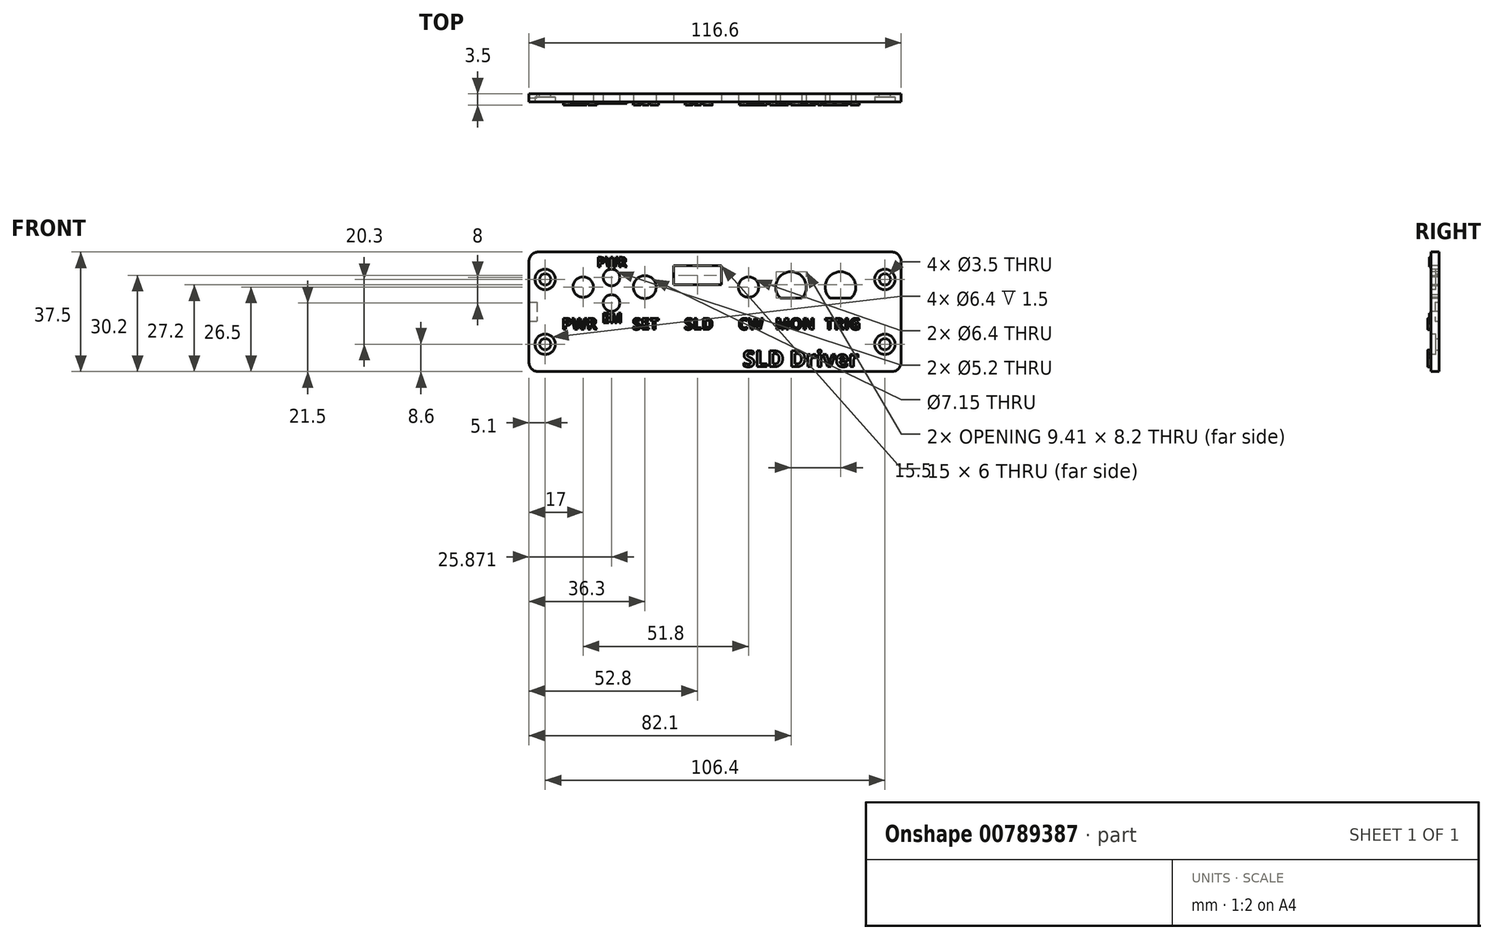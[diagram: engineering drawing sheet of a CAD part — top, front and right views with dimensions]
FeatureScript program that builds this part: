
annotation { "Feature Type Name" : "Feature", "Feature Type Description" : "" }
export const myFeature = defineFeature(function(context is Context, id is Id, definition is map)
    precondition{}
    {
        {
            var Q0;
            Q0=qCreatedBy(makeId("Front.planeOp"),FACE);
            var sketch = newSketch(context, id + "F0", { "sketchPlane" : qUnion([Q0])});
            skLineSegment(sketch, "E0.bottom", {"start": v(-55.3, 18.75) * mm, "end": v(55.3, 18.75) * mm});
            skLineSegment(sketch, "E0.top", {"start": v(-55.3, -18.75) * mm, "end": v(55.3, -18.75) * mm});
            skLineSegment(sketch, "E0.left", {"start": v(-58.3, 15.75) * mm, "end": v(-58.3, -15.75) * mm});
            skLineSegment(sketch, "E0.right", {"start": v(58.3, 15.75) * mm, "end": v(58.3, -15.75) * mm});
            skPoint(sketch, "E1.visualSharp", {"position": v(-58.3, 18.75) * mm});
            skArc(sketch, "E1.filletArc", {"start": v(-55.3, 18.75) * mm, "mid": v(-57.42, 17.87) * mm, "end": v(-58.3, 15.75) * mm});
            skPoint(sketch, "E2.visualSharp", {"position": v(58.3, 18.75) * mm});
            skArc(sketch, "E2.filletArc", {"start": v(58.3, 15.75) * mm, "mid": v(57.42, 17.87) * mm, "end": v(55.3, 18.75) * mm});
            skPoint(sketch, "E3.visualSharp", {"position": v(58.3, -18.75) * mm});
            skArc(sketch, "E3.filletArc", {"start": v(55.3, -18.75) * mm, "mid": v(57.42, -17.87) * mm, "end": v(58.3, -15.75) * mm});
            skPoint(sketch, "E4.visualSharp", {"position": v(-58.3, -18.75) * mm});
            skArc(sketch, "E4.filletArc", {"start": v(-58.3, -15.75) * mm, "mid": v(-57.42, -17.87) * mm, "end": v(-55.3, -18.75) * mm});
            skCircle(sketch, "E5", {"center": v(-53.2, 10.15) * mm, "radius": 1.75 * mm});
            skCircle(sketch, "E6", {"center": v(53.2, 10.15) * mm, "radius": 1.75 * mm});
            skCircle(sketch, "E7", {"center": v(-53.2, -10.15) * mm, "radius": 1.75 * mm});
            skCircle(sketch, "E8", {"center": v(53.2, -10.15) * mm, "radius": 1.75 * mm});
            skSolve(sketch);
        }
        {
            var Q0;
            Q0=makeQuery(id+"F0.imprint","IMPRINT",FACE,{"disambiguationData":[TD([[makeQuery(id+"F0.imprint","IMPRINT",EDGE,{"derivedFrom":sQuery(id+"F0.wireOp",EDGE,"E0.bottom")}),-1.0]])]});
            extrude(context, id + "F1", {"entities" : qUnion([Q0]), "depth" : 2.5 * mm});
        }
        {
            var Q0;
            Q0=makeQuery(id+"F1.opExtrude","CAP_FACE",FACE,{"disambiguationData":[OSD([sQuery(id+"F0.wireOp",EDGE,"E0.bottom"),sQuery(id+"F0.wireOp",EDGE,"E0.top"),sQuery(id+"F0.wireOp",EDGE,"E0.left"),sQuery(id+"F0.wireOp",EDGE,"E0.right"),sQuery(id+"F0.wireOp",EDGE,"E1.filletArc"),sQuery(id+"F0.wireOp",EDGE,"E2.filletArc"),sQuery(id+"F0.wireOp",EDGE,"E3.filletArc"),sQuery(id+"F0.wireOp",EDGE,"E4.filletArc"),sQuery(id+"F0.wireOp",EDGE,"E5"),sQuery(id+"F0.wireOp",EDGE,"E6"),sQuery(id+"F0.wireOp",EDGE,"E7"),sQuery(id+"F0.wireOp",EDGE,"E8")])],"isStart":false});
            var sketch = newSketch(context, id + "F2", { "sketchPlane" : qUnion([Q0])});
            skCircle(sketch, "E9", {"center": v(-53.2, 10.15) * mm, "radius": 3.2 * mm});
            skCircle(sketch, "E10", {"center": v(53.2, 10.15) * mm, "radius": 3.2 * mm});
            skCircle(sketch, "E11", {"center": v(-53.2, -10.15) * mm, "radius": 3.2 * mm});
            skCircle(sketch, "E12", {"center": v(53.2, -10.15) * mm, "radius": 3.2 * mm});
            skSolve(sketch);
        }
        {
            var Q0;
            Q0=qSketchRegion(id+"F2",true);
            extrude(context, id + "F3", {"entities" : qUnion([Q0]), "operationType" : NewBodyOperationType.REMOVE, "oppositeDirection" : true, "depth" : 1.5 * mm});
        }
        {
            var Q0;
            Q0=makeQuery(id+"F1.opExtrude","CAP_FACE",FACE,{"disambiguationData":[OSD([sQuery(id+"F0.wireOp",EDGE,"E0.bottom"),sQuery(id+"F0.wireOp",EDGE,"E0.top"),sQuery(id+"F0.wireOp",EDGE,"E0.left"),sQuery(id+"F0.wireOp",EDGE,"E0.right"),sQuery(id+"F0.wireOp",EDGE,"E1.filletArc"),sQuery(id+"F0.wireOp",EDGE,"E2.filletArc"),sQuery(id+"F0.wireOp",EDGE,"E3.filletArc"),sQuery(id+"F0.wireOp",EDGE,"E4.filletArc"),sQuery(id+"F0.wireOp",EDGE,"E5"),sQuery(id+"F0.wireOp",EDGE,"E6"),sQuery(id+"F0.wireOp",EDGE,"E7"),sQuery(id+"F0.wireOp",EDGE,"E8")])],"isStart":true});
            var sketch = newSketch(context, id + "F4", { "sketchPlane" : qUnion([Q0])});
            skLineSegment(sketch, "E13.bottom", {"start": v(58.3, 3) * mm, "end": v(55.8, 3) * mm});
            skLineSegment(sketch, "E13.top", {"start": v(58.3, -3) * mm, "end": v(55.8, -3) * mm});
            skLineSegment(sketch, "E13.left", {"start": v(58.3, 3) * mm, "end": v(58.3, -3) * mm});
            skLineSegment(sketch, "E13.right", {"start": v(55.8, 3) * mm, "end": v(55.8, -3) * mm});
            skSolve(sketch);
        }
        {
            var Q0;
            Q0=qSketchRegion(id+"F4",true);
            extrude(context, id + "F5", {"entities" : qUnion([Q0]), "operationType" : NewBodyOperationType.REMOVE, "oppositeDirection" : true, "depth" : 1.25 * mm});
        }
        {
            var Q0;
            Q0=makeQuery(id+"F1.opExtrude","CAP_FACE",FACE,{"disambiguationData":[OSD([sQuery(id+"F0.wireOp",EDGE,"E0.bottom"),sQuery(id+"F0.wireOp",EDGE,"E0.top"),sQuery(id+"F0.wireOp",EDGE,"E0.left"),sQuery(id+"F0.wireOp",EDGE,"E0.right"),sQuery(id+"F0.wireOp",EDGE,"E1.filletArc"),sQuery(id+"F0.wireOp",EDGE,"E2.filletArc"),sQuery(id+"F0.wireOp",EDGE,"E3.filletArc"),sQuery(id+"F0.wireOp",EDGE,"E4.filletArc"),sQuery(id+"F0.wireOp",EDGE,"E5"),sQuery(id+"F0.wireOp",EDGE,"E6"),sQuery(id+"F0.wireOp",EDGE,"E7"),sQuery(id+"F0.wireOp",EDGE,"E8")])],"isStart":false});
            var sketch = newSketch(context, id + "F6", { "sketchPlane" : qUnion([Q0])});
            skLineSegment(sketch, "E14", {"start": v(-63.46, 7.75) * mm, "end": v(64.15, 7.75) * mm, "construction": true});
            skArc(sketch, "E15", {"start": v(42.69, 4.35) * mm, "mid": v(39.3, 12.55) * mm, "end": v(35.91, 4.35) * mm});
            skLineSegment(sketch, "E16", {"start": v(-48.3, 18.75) * mm, "end": v(-48.3, -12.75) * mm, "construction": true});
            skLineSegment(sketch, "E17", {"start": v(48.3, -12.75) * mm, "end": v(48.3, 18.75) * mm, "construction": true});
            skLineSegment(sketch, "E18.trimOffspring", {"start": v(35.91, 4.35) * mm, "end": v(42.69, 4.35) * mm});
            skCircle(sketch, "E19", {"center": v(-22, 7.75) * mm, "radius": 3.58 * mm});
            skPoint(sketch, "E20", {"position": v(0.34, 7.75) * mm});
            skCircle(sketch, "E21", {"center": v(10.5, 7.75) * mm, "radius": 3.2 * mm});
            skLineSegment(sketch, "E22", {"start": v(-71.06, -1.55) * mm, "end": v(67.35, -1.55) * mm, "construction": true});
            skLineSegment(sketch, "E23", {"start": v(-66.45, 8.45) * mm, "end": v(18.57, 8.45) * mm, "construction": true});
            skLineSegment(sketch, "E24.bottom", {"start": v(-13, 8.45) * mm, "end": v(2, 8.45) * mm});
            skLineSegment(sketch, "E24.top", {"start": v(-13, 14.45) * mm, "end": v(2, 14.45) * mm});
            skLineSegment(sketch, "E24.left", {"start": v(-13, 8.45) * mm, "end": v(-13, 14.45) * mm});
            skLineSegment(sketch, "E24.right", {"start": v(2, 8.45) * mm, "end": v(2, 14.45) * mm});
            skArc(sketch, "E25", {"start": v(27.19, 4.35) * mm, "mid": v(23.8, 12.55) * mm, "end": v(20.41, 4.35) * mm});
            skLineSegment(sketch, "E26.trimOffspring", {"start": v(20.41, 4.35) * mm, "end": v(27.19, 4.35) * mm});
            skLineSegment(sketch, "E27", {"start": v(-32.43, 24.6) * mm, "end": v(-32.43, -13.66) * mm, "construction": true});
            skCircle(sketch, "E28", {"center": v(-41.3, 7.75) * mm, "radius": 3.2 * mm});
            skCircle(sketch, "E29", {"center": v(-32.43, 10.75) * mm, "radius": 2.6 * mm});
            skCircle(sketch, "E30", {"center": v(-32.43, 2.75) * mm, "radius": 2.6 * mm});
            skCircle(sketch, "E31", {"center": v(-22, 7.75) * mm, "radius": 5.25 * mm, "construction": true});
            skSolve(sketch);
        }
        {
            var Q0;
            Q0=qSketchRegion(id+"F6",true);
            extrude(context, id + "F7", {"entities" : qUnion([Q0]), "operationType" : NewBodyOperationType.REMOVE, "endBound" : BoundingType.THROUGH_ALL, "oppositeDirection" : true, "depth" : 25 * mm});
        }
        {
            var Q0;
            Q0=makeQuery(id+"F1.opExtrude","CAP_FACE",FACE,{"disambiguationData":[OSD([sQuery(id+"F0.wireOp",EDGE,"E0.bottom"),sQuery(id+"F0.wireOp",EDGE,"E0.top"),sQuery(id+"F0.wireOp",EDGE,"E0.left"),sQuery(id+"F0.wireOp",EDGE,"E0.right"),sQuery(id+"F0.wireOp",EDGE,"E1.filletArc"),sQuery(id+"F0.wireOp",EDGE,"E2.filletArc"),sQuery(id+"F0.wireOp",EDGE,"E3.filletArc"),sQuery(id+"F0.wireOp",EDGE,"E4.filletArc"),sQuery(id+"F0.wireOp",EDGE,"E5"),sQuery(id+"F0.wireOp",EDGE,"E6"),sQuery(id+"F0.wireOp",EDGE,"E7"),sQuery(id+"F0.wireOp",EDGE,"E8")])],"isStart":false});
            var sketch = newSketch(context, id + "F8", { "sketchPlane" : qUnion([Q0])});
            skText(sketch, "E32", { "text": "PWR", "fontName": "OpenSans-Bold.ttf"});
            skLineSegment(sketch, "E33", {"start": v(-84.62, -5.52) * mm, "end": v(84.91, -5.52) * mm, "construction": true});
            skText(sketch, "E34", { "text": "SET", "fontName": "OpenSans-Bold.ttf"});
            skText(sketch, "E35", { "text": "SLD", "fontName": "OpenSans-Bold.ttf"});
            skText(sketch, "E36", { "text": "CW   MON", "fontName": "OpenSans-Bold.ttf"});
            skText(sketch, "E37", { "text": "TRIG", "fontName": "OpenSans-Bold.ttf"});
            const initialGuessF8  = {"E32": [-0.0479, -0.00552, 1, 0, 0.0035], "E34": [-0.02585, -0.00552, 1, 0, 0.0035], "E35": [-0.0096, -0.00552, 1, 0, 0.0035], "E36": [0.00727, -0.00552, 1, 0, 0.0035], "E37": [0.03443, -0.00552, 1, 0, 0.0035]};
            skSetInitialGuess(sketch, initialGuessF8);
            skSolve(sketch);
        }
        {
            var Q0;
            Q0=qSketchRegion(id+"F8",true);
            extrude(context, id + "F9", {"entities" : qUnion([Q0]), "operationType" : NewBodyOperationType.ADD, "depth" : 1 * mm});
        }
        {
            var Q0;
            {var subQ70=sQuery(id+"F0.wireOp",EDGE,"E0.right");var subQ114=sQuery(id+"F0.wireOp",EDGE,"E3.filletArc");var subQ120=sQuery(id+"F0.wireOp",EDGE,"E4.filletArc");var subQ132=sQuery(id+"F0.wireOp",EDGE,"E1.filletArc");var subQ140=sQuery(id+"F0.wireOp",EDGE,"E0.top");var subQ143=sQuery(id+"F0.wireOp",EDGE,"E0.left");var subQ152=sQuery(id+"F0.wireOp",EDGE,"E2.filletArc");var subQ182=sQuery(id+"F0.wireOp",EDGE,"E0.bottom");var subQ183=makeQuery(id+"F1.opExtrude","SWEPT_FACE",FACE,{"disambiguationData":[OSD([subQ182])]});Q0=makeQuery(id+"Fu2jKsRN7ARvOCH_1.boolean.opBoolean","SPLIT",FACE,{"disambiguationData":[TD([subQ183])],"derivedFrom":makeQuery(id+"F9.boolean.opBoolean","SPLIT",FACE,{"disambiguationData":[TD([subQ183])],"derivedFrom":makeQuery(id+"F1.opExtrude","CAP_FACE",FACE,{"disambiguationData":[OSD([subQ182,subQ140,subQ143,subQ70,subQ132,subQ152,subQ114,subQ120,sQuery(id+"F0.wireOp",EDGE,"E5"),sQuery(id+"F0.wireOp",EDGE,"E6"),sQuery(id+"F0.wireOp",EDGE,"E7"),sQuery(id+"F0.wireOp",EDGE,"E8")])],"isStart":false})})});}
            var sketch = newSketch(context, id + "F10", { "sketchPlane" : qUnion([Q0])});
            skText(sketch, "E38", { "text": "SLD Driver", "fontName": "OpenSans-Bold.ttf"});
            const initialGuessF10  = {"E38": [0.00869, -0.0172, 1, 0, 0.005]};
            skSetInitialGuess(sketch, initialGuessF10);
            skSolve(sketch);
        }
        {
            var Q0;
            Q0=qSketchRegion(id+"F10",true);
            extrude(context, id + "F11", {"entities" : qUnion([Q0]), "operationType" : NewBodyOperationType.ADD, "depth" : 1 * mm});
        }
        {
            var Q0;
            {var subQ22=sQuery(id+"F0.wireOp",EDGE,"E2.filletArc");var subQ26=sQuery(id+"F0.wireOp",EDGE,"E0.bottom");var subQ27=makeQuery(id+"F1.opExtrude","SWEPT_FACE",FACE,{"disambiguationData":[OSD([subQ26])]});var subQ111=sQuery(id+"F0.wireOp",EDGE,"E0.top");var subQ184=sQuery(id+"F0.wireOp",EDGE,"E0.left");var subQ187=sQuery(id+"F0.wireOp",EDGE,"E0.right");var subQ190=sQuery(id+"F0.wireOp",EDGE,"E1.filletArc");var subQ194=sQuery(id+"F0.wireOp",EDGE,"E3.filletArc");var subQ197=sQuery(id+"F0.wireOp",EDGE,"E4.filletArc");Q0=makeQuery(id+"F11.boolean.opBoolean","SPLIT",FACE,{"disambiguationData":[TD([subQ27])],"derivedFrom":makeQuery(id+"F9.boolean.opBoolean","SPLIT",FACE,{"disambiguationData":[TD([subQ27])],"derivedFrom":makeQuery(id+"F1.opExtrude","CAP_FACE",FACE,{"disambiguationData":[OSD([subQ26,subQ111,subQ184,subQ187,subQ190,subQ22,subQ194,subQ197,sQuery(id+"F0.wireOp",EDGE,"E5"),sQuery(id+"F0.wireOp",EDGE,"E6"),sQuery(id+"F0.wireOp",EDGE,"E7"),sQuery(id+"F0.wireOp",EDGE,"E8")])],"isStart":false})})});}
            var sketch = newSketch(context, id + "F12", { "sketchPlane" : qUnion([Q0])});
            skText(sketch, "E39", { "text": "PWR", "fontName": "OpenSans-Bold.ttf"});
            skText(sketch, "E40", { "text": "EM", "fontName": "OpenSans-Bold.ttf"});
            const initialGuessF12  = {"E39": [-0.037, 0.01409, 1, 0, 0.003], "E40": [-0.03532, -0.00341, 1, 0, 0.003]};
            skSetInitialGuess(sketch, initialGuessF12);
            skSolve(sketch);
        }
        {
            var Q0;
            Q0 = qSketchRegion(id + "F12", true);
            extrude(context, id + "F13", {"entities" : qUnion([Q0]), "operationType" : NewBodyOperationType.ADD, "depth" : 0.5 * mm, "offsetDistance" : 25 * mm});
        }
    });
